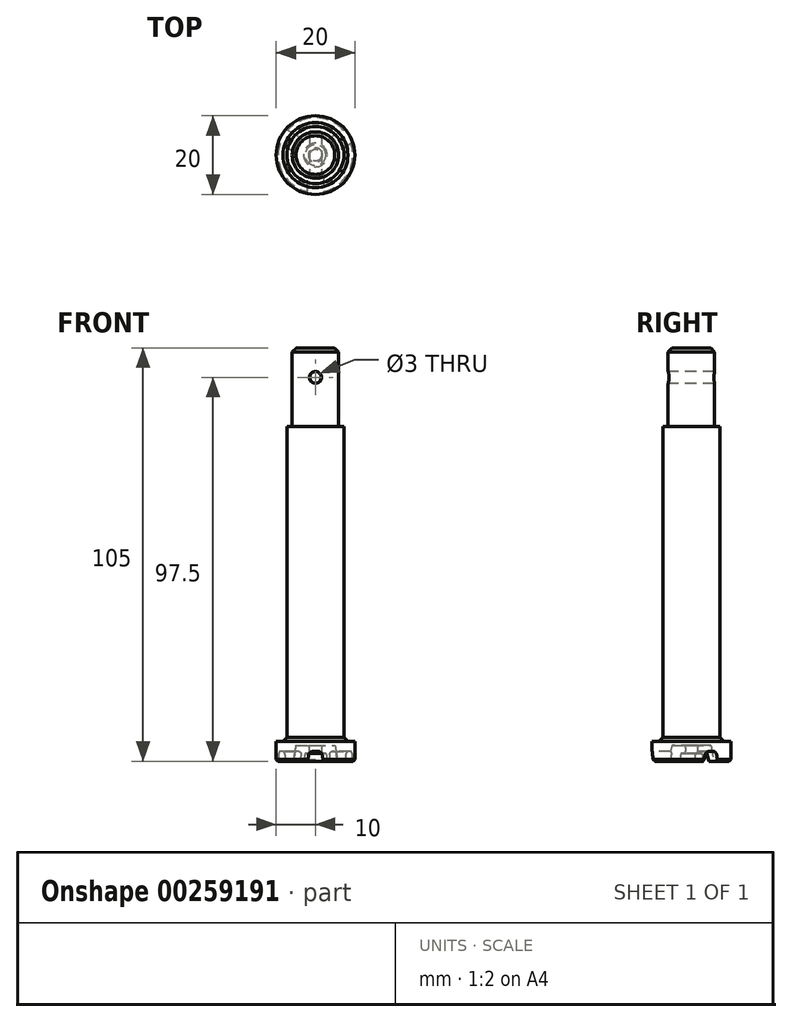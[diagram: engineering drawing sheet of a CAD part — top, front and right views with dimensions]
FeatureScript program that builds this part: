
annotation { "Feature Type Name" : "Feature", "Feature Type Description" : "" }
export const myFeature = defineFeature(function(context is Context, id is Id, definition is map)
    precondition{}
    {
        {
            var Q0;
            Q0=qCreatedBy(makeId("Top.planeOp"),FACE);
            var sketch = newSketch(context, id + "F0", { "sketchPlane" : qUnion([Q0])});
            skCircle(sketch, "E0", {"center": v(0, 0) * mm, "radius": 10 * mm});
            skCircle(sketch, "E1", {"center": v(0, 0) * mm, "radius": 1.5 * mm});
            skCircle(sketch, "E2", {"center": v(0, 0) * mm, "radius": 3 * mm});
            skCircle(sketch, "E3", {"center": v(0, 0) * mm, "radius": 5 * mm});
            skLineSegment(sketch, "E4", {"start": v(0, -5) * mm, "end": v(0, -10) * mm, "construction": true});
            skLineSegment(sketch, "E5", {"start": v(-2, -4.58) * mm, "end": v(-2, -9.8) * mm});
            skLineSegment(sketch, "E6", {"start": v(2, -4.58) * mm, "end": v(2, -9.8) * mm});
            skLineSegment(sketch, "E7.1.0", {"start": v(4.97, 0.56) * mm, "end": v(9.49, 3.17) * mm});
            skLineSegment(sketch, "E7.1.1", {"start": v(2.97, 4.02) * mm, "end": v(7.49, 6.63) * mm});
            skLineSegment(sketch, "E7.1.2", {"start": v(4.33, 2.5) * mm, "end": v(8.66, 5) * mm, "construction": true});
            skLineSegment(sketch, "E7.2.0", {"start": v(-2.97, 4.02) * mm, "end": v(-7.49, 6.63) * mm});
            skLineSegment(sketch, "E7.2.1", {"start": v(-4.97, 0.56) * mm, "end": v(-9.49, 3.17) * mm});
            skLineSegment(sketch, "E7.2.2", {"start": v(-4.33, 2.5) * mm, "end": v(-8.66, 5) * mm, "construction": true});
            skLineSegment(sketch, "E8", {"start": v(-2, -4.58) * mm, "end": v(-2, -3.7) * mm});
            skLineSegment(sketch, "E9", {"start": v(-2, -3.7) * mm, "end": v(2, -3.7) * mm});
            skLineSegment(sketch, "E10", {"start": v(2, -3.7) * mm, "end": v(2, -4.58) * mm});
            skLineSegment(sketch, "E11", {"start": v(-2, -9.8) * mm, "end": v(-2, -10.8) * mm});
            skLineSegment(sketch, "E12", {"start": v(-2, -10.8) * mm, "end": v(2, -10.8) * mm});
            skLineSegment(sketch, "E13", {"start": v(2, -10.8) * mm, "end": v(2, -9.8) * mm});
            skLineSegment(sketch, "E14.1.0", {"start": v(4.97, 0.56) * mm, "end": v(4.2, 0.12) * mm});
            skLineSegment(sketch, "E14.1.1", {"start": v(4.2, 0.12) * mm, "end": v(2.2, 3.58) * mm});
            skLineSegment(sketch, "E14.1.2", {"start": v(2.2, 3.58) * mm, "end": v(2.97, 4.02) * mm});
            skLineSegment(sketch, "E14.1.3", {"start": v(8.35, 7.13) * mm, "end": v(7.49, 6.63) * mm});
            skLineSegment(sketch, "E14.1.4", {"start": v(10.35, 3.67) * mm, "end": v(8.35, 7.13) * mm});
            skLineSegment(sketch, "E14.1.5", {"start": v(9.49, 3.17) * mm, "end": v(10.35, 3.67) * mm});
            skLineSegment(sketch, "E14.2.0", {"start": v(-2.97, 4.02) * mm, "end": v(-2.2, 3.58) * mm});
            skLineSegment(sketch, "E14.2.1", {"start": v(-2.2, 3.58) * mm, "end": v(-4.2, 0.12) * mm});
            skLineSegment(sketch, "E14.2.2", {"start": v(-4.2, 0.12) * mm, "end": v(-4.97, 0.56) * mm});
            skLineSegment(sketch, "E14.2.3", {"start": v(-10.35, 3.67) * mm, "end": v(-9.49, 3.17) * mm});
            skLineSegment(sketch, "E14.2.4", {"start": v(-8.35, 7.13) * mm, "end": v(-10.35, 3.67) * mm});
            skLineSegment(sketch, "E14.2.5", {"start": v(-7.49, 6.63) * mm, "end": v(-8.35, 7.13) * mm});
            skSolve(sketch);
        }
        {
            var Q0;
            Q0=qCreatedBy(makeId("Front.planeOp"),FACE);
            var sketch = newSketch(context, id + "F1", { "sketchPlane" : qUnion([Q0])});
            skLineSegment(sketch, "E15", {"start": v(0, 0) * mm, "end": v(0, 105) * mm});
            skLineSegment(sketch, "E16", {"start": v(-10, 0) * mm, "end": v(-10, 5) * mm});
            skLineSegment(sketch, "E17", {"start": v(-10, 5) * mm, "end": v(-8.25, 5) * mm});
            skLineSegment(sketch, "E18", {"start": v(-7.25, 5) * mm, "end": v(-7.25, 6) * mm, "construction": true});
            skLineSegment(sketch, "E19", {"start": v(0, 105) * mm, "end": v(-5.9, 105) * mm});
            skLineSegment(sketch, "E20", {"start": v(-5.9, 105) * mm, "end": v(-5.9, 85) * mm});
            skLineSegment(sketch, "E21", {"start": v(-5.9, 85) * mm, "end": v(-7.25, 85) * mm});
            skCircle(sketch, "E22", {"center": v(0, 97.5) * mm, "radius": 1.5 * mm});
            skLineSegment(sketch, "E23", {"start": v(-3, 0) * mm, "end": v(-3, 2) * mm, "construction": true});
            skLineSegment(sketch, "E24", {"start": v(-3, 2) * mm, "end": v(-1.5, 2) * mm});
            skLineSegment(sketch, "E25", {"start": v(-1.5, 2) * mm, "end": v(-1.5, 4) * mm, "construction": true});
            skLineSegment(sketch, "E26", {"start": v(-1.5, 4) * mm, "end": v(-5, 4) * mm});
            skLineSegment(sketch, "E27", {"start": v(-5, 4) * mm, "end": v(-5.7, 0) * mm});
            skLineSegment(sketch, "E28", {"start": v(-1.5, 2) * mm, "end": v(-1.5, 0) * mm, "construction": true});
            skLineSegment(sketch, "E29", {"start": v(-5.7, 0) * mm, "end": v(-10, 0) * mm});
            skLineSegment(sketch, "E30", {"start": v(-5, 4) * mm, "end": v(-5, 0) * mm, "construction": true});
            skLineSegment(sketch, "E31", {"start": v(-3, 0) * mm, "end": v(-2.65, 2) * mm});
            skArc(sketch, "E32", {"start": v(-1.8, 2) * mm, "mid": v(-1.5, 3) * mm, "end": v(-1.8, 4) * mm});
            skLineSegment(sketch, "E33", {"start": v(-8.25, 5) * mm, "end": v(-7.25, 6) * mm});
            skLineSegment(sketch, "E34", {"start": v(-7.25, 6) * mm, "end": v(-7.25, 85) * mm});
            skLineSegment(sketch, "E35", {"start": v(-8.25, 5) * mm, "end": v(-7.25, 5) * mm, "construction": true});
            skLineSegment(sketch, "E36", {"start": v(-3, 0) * mm, "end": v(0, 0) * mm});
            skSolve(sketch);
        }
        {
            var Q0;
            Q0 = qSketchRegion(id + "F1", true);
            var Q1;
            Q1=sQuery(id+"F1.wireOp",EDGE,"E15");
            revolve(context, id + "F2", {"entities" : qUnion([Q0]), "axis" : qUnion([Q1]), "revolveType" : RevolveType.FULL});
        }
        {
            var Q0;
            {var subQ0=sQuery(id+"F1.wireOp",EDGE,"E22");var subQ1=sQuery(id+"F1.wireOp",EDGE,"E15");var subQ2=makeQuery(id+"F1.imprint","INTERSECT",VERTEX,{"disambiguationData":[OD(0.0)],"derivedFrom":[subQ1,subQ0]});Q0=makeQuery(id+"F1.imprint","IMPRINT",FACE,{"disambiguationData":[TD([[makeQuery(id+"F1.imprint","IMPRINT",EDGE,{"disambiguationData":[TD([[subQ2,-1.0]])],"derivedFrom":subQ1}),-1.0]])]});}
            var Q1;
            {var subQ0=sQuery(id+"F1.wireOp",EDGE,"E22");var subQ1=sQuery(id+"F1.wireOp",EDGE,"E15");var subQ2=makeQuery(id+"F1.imprint","INTERSECT",VERTEX,{"disambiguationData":[OD(0.0)],"derivedFrom":[subQ1,subQ0]});Q1=makeQuery(id+"F1.imprint","IMPRINT",FACE,{"disambiguationData":[TD([[makeQuery(id+"F1.imprint","IMPRINT",EDGE,{"disambiguationData":[TD([[subQ2,-1.0]])],"derivedFrom":subQ1}),1.0]])]});}
            extrude(context, id + "F3", {"entities" : qUnion([Q0, Q1]), "operationType" : NewBodyOperationType.REMOVE, "endBound" : BoundingType.SYMMETRIC, "oppositeDirection" : true, "depth" : 25 * mm});
        }
        {
            var Q0;
            Q0=makeQuery(id+"F2.opRevolve","SWEPT_EDGE",EDGE,{"disambiguationData":[OSD([sQuery(id+"F1.wireOp",EDGE,"E19"),sQuery(id+"F1.wireOp",EDGE,"E20")])]});
            chamfer(context, id + "F4", {"entities" : qUnion([Q0]), "width" : 1 * mm, "tangentPropagation" : true});
        }
        {
            var Q0;
            {var subQ0=sQuery(id+"F0.wireOp",EDGE,"E5");Q0=makeQuery(id+"F0.imprint","IMPRINT",FACE,{"disambiguationData":[TD([[makeQuery(id+"F0.imprint","IMPRINT",EDGE,{"derivedFrom":subQ0}),1.0]])]});}
            var Q1;
            {var subQ0=sQuery(id+"F0.wireOp",EDGE,"E11");Q1=makeQuery(id+"F0.imprint","IMPRINT",FACE,{"disambiguationData":[TD([[makeQuery(id+"F0.imprint","IMPRINT",EDGE,{"derivedFrom":subQ0}),1.0]])]});}
            var Q2;
            {var subQ0=sQuery(id+"F0.wireOp",EDGE,"E8");Q2=makeQuery(id+"F0.imprint","IMPRINT",FACE,{"disambiguationData":[TD([[makeQuery(id+"F0.imprint","IMPRINT",EDGE,{"derivedFrom":subQ0}),-1.0]])]});}
            var Q3;
            {var subQ0=sQuery(id+"F0.wireOp",EDGE,"E14.2.0");Q3=makeQuery(id+"F0.imprint","IMPRINT",FACE,{"disambiguationData":[TD([[makeQuery(id+"F0.imprint","IMPRINT",EDGE,{"derivedFrom":subQ0}),-1.0]])]});}
            var Q4;
            {var subQ0=sQuery(id+"F0.wireOp",EDGE,"E14.1.0");Q4=makeQuery(id+"F0.imprint","IMPRINT",FACE,{"disambiguationData":[TD([[makeQuery(id+"F0.imprint","IMPRINT",EDGE,{"derivedFrom":subQ0}),-1.0]])]});}
            var Q5;
            {var subQ0=sQuery(id+"F0.wireOp",EDGE,"E7.1.0");Q5=makeQuery(id+"F0.imprint","IMPRINT",FACE,{"disambiguationData":[TD([[makeQuery(id+"F0.imprint","IMPRINT",EDGE,{"derivedFrom":subQ0}),1.0]])]});}
            var Q6;
            {var subQ2=sQuery(id+"F0.wireOp",EDGE,"E14.1.3");Q6=makeQuery(id+"F0.imprint","IMPRINT",FACE,{"disambiguationData":[TD([[makeQuery(id+"F0.imprint","IMPRINT",EDGE,{"derivedFrom":subQ2}),1.0]])]});}
            var Q7;
            {var subQ0=sQuery(id+"F0.wireOp",EDGE,"E7.2.0");Q7=makeQuery(id+"F0.imprint","IMPRINT",FACE,{"disambiguationData":[TD([[makeQuery(id+"F0.imprint","IMPRINT",EDGE,{"derivedFrom":subQ0}),1.0]])]});}
            var Q8;
            {var subQ2=sQuery(id+"F0.wireOp",EDGE,"E14.2.3");Q8=makeQuery(id+"F0.imprint","IMPRINT",FACE,{"disambiguationData":[TD([[makeQuery(id+"F0.imprint","IMPRINT",EDGE,{"derivedFrom":subQ2}),1.0]])]});}
            extrude(context, id + "F5", {"entities" : qUnion([Q0, Q1, Q2, Q3, Q4, Q5, Q6, Q7, Q8]), "operationType" : NewBodyOperationType.REMOVE, "depth" : 2.5 * mm, "hasDraft" : true, "draftAngle" : 10 * degree, "draftPullDirection" : true});
        }
        {
            var Q0;
            Q0=makeQuery(id+"F5.boolean.opBoolean","COPY",EDGE,{"derivedFrom":makeQuery(id+"F5.opExtrude","CAP_EDGE",EDGE,{"disambiguationData":[OSD([sQuery(id+"F0.wireOp",EDGE,"E7.2.1"),sQuery(id+"F0.wireOp",EDGE,"E14.2.2"),sQuery(id+"F0.wireOp",EDGE,"E14.2.3")])],"isStart":false})});
            var Q1;
            Q1=makeQuery(id+"F5.boolean.opBoolean","COPY",EDGE,{"derivedFrom":makeQuery(id+"F5.opExtrude","CAP_EDGE",EDGE,{"disambiguationData":[OSD([sQuery(id+"F0.wireOp",EDGE,"E7.2.0"),sQuery(id+"F0.wireOp",EDGE,"E14.2.0"),sQuery(id+"F0.wireOp",EDGE,"E14.2.5")])],"isStart":false})});
            var Q2;
            Q2=makeQuery(id+"F5.boolean.opBoolean","COPY",EDGE,{"derivedFrom":makeQuery(id+"F5.opExtrude","CAP_EDGE",EDGE,{"disambiguationData":[OSD([sQuery(id+"F0.wireOp",EDGE,"E7.1.0"),sQuery(id+"F0.wireOp",EDGE,"E14.1.0"),sQuery(id+"F0.wireOp",EDGE,"E14.1.5")])],"isStart":false})});
            var Q3;
            Q3=makeQuery(id+"F5.boolean.opBoolean","COPY",EDGE,{"derivedFrom":makeQuery(id+"F5.opExtrude","CAP_EDGE",EDGE,{"disambiguationData":[OSD([sQuery(id+"F0.wireOp",EDGE,"E6"),sQuery(id+"F0.wireOp",EDGE,"E10"),sQuery(id+"F0.wireOp",EDGE,"E13")])],"isStart":false})});
            var Q4;
            Q4=makeQuery(id+"F5.boolean.opBoolean","COPY",EDGE,{"derivedFrom":makeQuery(id+"F5.opExtrude","CAP_EDGE",EDGE,{"disambiguationData":[OSD([sQuery(id+"F0.wireOp",EDGE,"E5"),sQuery(id+"F0.wireOp",EDGE,"E8"),sQuery(id+"F0.wireOp",EDGE,"E11")])],"isStart":false})});
            var Q5;
            Q5=makeQuery(id+"F5.boolean.opBoolean","COPY",EDGE,{"derivedFrom":makeQuery(id+"F5.opExtrude","CAP_EDGE",EDGE,{"disambiguationData":[OSD([sQuery(id+"F0.wireOp",EDGE,"E7.1.1"),sQuery(id+"F0.wireOp",EDGE,"E14.1.2"),sQuery(id+"F0.wireOp",EDGE,"E14.1.3")])],"isStart":false})});
            fillet(context, id + "F6", {"entities" : qUnion([Q0, Q1, Q2, Q3, Q4, Q5]), "radius" : 1 * mm, "tangentPropagation" : true, "rho" : 0.3, "crossSection" : FilletCrossSection.CONIC, "allowEdgeOverflow" : false});
        }
        {
            var Q0;
            {var subQ0=sQuery(id+"F1.wireOp",EDGE,"E16");var subQ1=sQuery(id+"F1.wireOp",EDGE,"E29");Q0=makeQuery(id+"F5.boolean.opBoolean","SPLIT",EDGE,{"disambiguationData":[TD([makeQuery(id+"F5.opExtrude","SWEPT_FACE",FACE,{"disambiguationData":[OSD([sQuery(id+"F0.wireOp",EDGE,"E7.1.1"),sQuery(id+"F0.wireOp",EDGE,"E14.1.2"),sQuery(id+"F0.wireOp",EDGE,"E14.1.3")])]})])],"derivedFrom":makeQuery(id+"F2.opRevolve","SWEPT_EDGE",EDGE,{"disambiguationData":[OSD([subQ0,subQ1])]})});}
            var Q1;
            {var subQ0=sQuery(id+"F1.wireOp",EDGE,"E16");var subQ1=sQuery(id+"F1.wireOp",EDGE,"E29");Q1=makeQuery(id+"F5.boolean.opBoolean","SPLIT",EDGE,{"disambiguationData":[TD([makeQuery(id+"F5.opExtrude","SWEPT_FACE",FACE,{"disambiguationData":[OSD([sQuery(id+"F0.wireOp",EDGE,"E5"),sQuery(id+"F0.wireOp",EDGE,"E8"),sQuery(id+"F0.wireOp",EDGE,"E11")])]})])],"derivedFrom":makeQuery(id+"F2.opRevolve","SWEPT_EDGE",EDGE,{"disambiguationData":[OSD([subQ0,subQ1])]})});}
            var Q2;
            {var subQ0=sQuery(id+"F1.wireOp",EDGE,"E16");var subQ1=sQuery(id+"F1.wireOp",EDGE,"E29");Q2=makeQuery(id+"F5.boolean.opBoolean","SPLIT",EDGE,{"disambiguationData":[TD([makeQuery(id+"F5.opExtrude","SWEPT_FACE",FACE,{"disambiguationData":[OSD([sQuery(id+"F0.wireOp",EDGE,"E6"),sQuery(id+"F0.wireOp",EDGE,"E10"),sQuery(id+"F0.wireOp",EDGE,"E13")])]})])],"derivedFrom":makeQuery(id+"F2.opRevolve","SWEPT_EDGE",EDGE,{"disambiguationData":[OSD([subQ0,subQ1])]})});}
            chamfer(context, id + "F7", {"entities" : qUnion([Q0, Q1, Q2]), "width" : 0.5 * mm, "tangentPropagation" : true});
        }
    });
